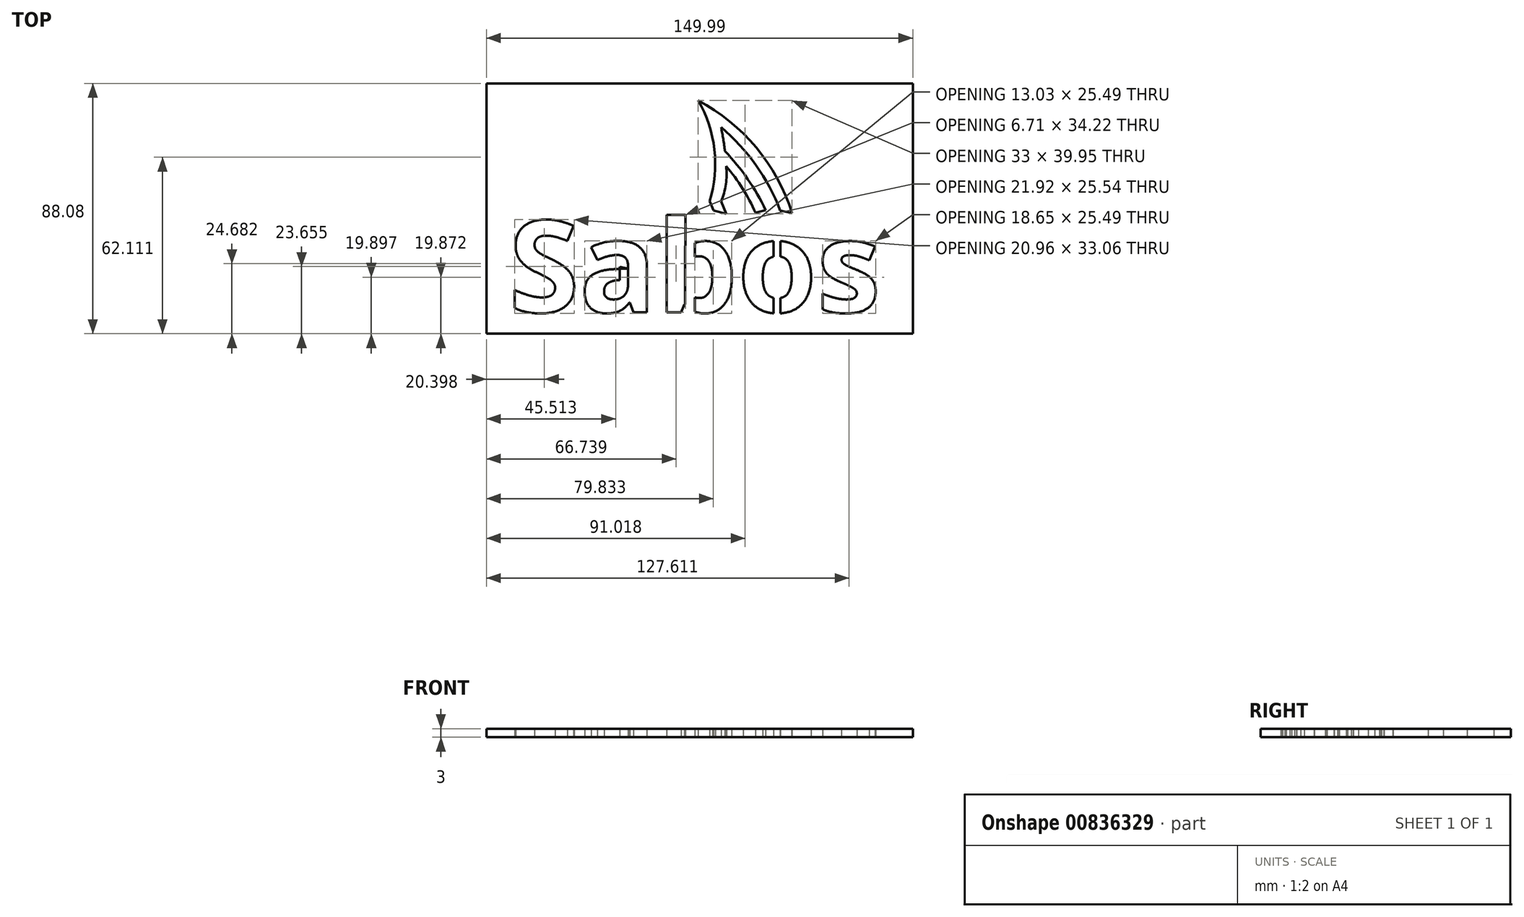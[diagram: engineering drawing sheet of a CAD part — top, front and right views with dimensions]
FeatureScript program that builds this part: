
annotation { "Feature Type Name" : "Feature", "Feature Type Description" : "" }
export const myFeature = defineFeature(function(context is Context, id is Id, definition is map)
    precondition{}
    {
        {
            var Q0;
            Q0=qCreatedBy(makeId("Top.planeOp"),FACE);
            var sketch = newSketch(context, id + "F0", { "sketchPlane" : qUnion([Q0])});
            skText(sketch, "E0", { "text": "Sabos", "fontName": "OpenSans-Bold.ttf"});
            skLineSegment(sketch, "E1", {"start": v(7.5, -7.38) * mm, "end": v(11.9, -8.54) * mm});
            skLineSegment(sketch, "E2", {"start": v(11.9, -8.54) * mm, "end": v(10.1, -4.19) * mm});
            skLineSegment(sketch, "E3", {"start": v(7.5, -7.38) * mm, "end": v(6.07, -4.03) * mm});
            skLineSegment(sketch, "E4", {"start": v(22.19, -8.14) * mm, "end": v(25.78, -7.18) * mm});
            skLineSegment(sketch, "E5", {"start": v(30.88, -7.34) * mm, "end": v(35.03, -8.18) * mm});
            skArc(sketch, "E6", {"start": v(6.07, -4.03) * mm, "mid": v(7.74, 14.12) * mm, "end": v(2.03, 31.42) * mm});
            skArc(sketch, "E7", {"start": v(35.03, -8.18) * mm, "mid": v(22.4, 14.85) * mm, "end": v(2.03, 31.42) * mm});
            skArc(sketch, "E8", {"start": v(30.88, -7.34) * mm, "mid": v(22.34, 8.62) * mm, "end": v(10.1, 21.97) * mm});
            skArc(sketch, "E9", {"start": v(25.78, -7.18) * mm, "mid": v(19.43, 3.78) * mm, "end": v(11.42, 13.58) * mm});
            skArc(sketch, "E10", {"start": v(22.19, -8.14) * mm, "mid": v(17.61, 0.41) * mm, "end": v(11.89, 8.24) * mm});
            skArc(sketch, "E11", {"start": v(11.42, 13.58) * mm, "mid": v(10.85, 17.79) * mm, "end": v(10.1, 21.97) * mm});
            skArc(sketch, "E12", {"start": v(10.1, -4.19) * mm, "mid": v(11.78, 1.91) * mm, "end": v(11.89, 8.24) * mm});
            skLineSegment(sketch, "E13.bottom", {"start": v(-72.5, -50.67) * mm, "end": v(77.5, -50.67) * mm});
            skLineSegment(sketch, "E13.top", {"start": v(-72.5, 37.4) * mm, "end": v(77.5, 37.4) * mm});
            skLineSegment(sketch, "E13.left", {"start": v(-72.5, -50.67) * mm, "end": v(-72.5, 37.4) * mm});
            skLineSegment(sketch, "E13.right", {"start": v(77.5, -50.67) * mm, "end": v(77.5, 37.4) * mm});
            skLineSegment(sketch, "E14", {"start": v(-22.68, -27.79) * mm, "end": v(-22.68, -32.66) * mm});
            skLineSegment(sketch, "E15", {"start": v(-22.68, -32.66) * mm, "end": v(-25.59, -32.66) * mm});
            skLineSegment(sketch, "E16", {"start": v(-25.59, -32.66) * mm, "end": v(-25.59, -27.2) * mm});
            skLineSegment(sketch, "E17", {"start": v(-25.59, -27.2) * mm, "end": v(-22.68, -27.79) * mm});
            skLineSegment(sketch, "E18", {"start": v(-2.57, -17.96) * mm, "end": v(-2.57, -45.1) * mm});
            skLineSegment(sketch, "E19", {"start": v(-2.57, -45.1) * mm, "end": v(0.83, -45.77) * mm});
            skLineSegment(sketch, "E20", {"start": v(0.83, -45.77) * mm, "end": v(0.83, -17.64) * mm});
            skLineSegment(sketch, "E21", {"start": v(0.83, -17.64) * mm, "end": v(-2.57, -17.96) * mm});
            skLineSegment(sketch, "E22", {"start": v(29.75, -15.5) * mm, "end": v(29.75, -46.16) * mm, "construction": true});
            skLineSegment(sketch, "E23", {"start": v(29.75, -15.5) * mm, "end": v(28.6, -15.5) * mm});
            skLineSegment(sketch, "E24", {"start": v(28.6, -15.5) * mm, "end": v(28.6, -46.25) * mm});
            skLineSegment(sketch, "E25", {"start": v(28.6, -46.25) * mm, "end": v(29.75, -46.16) * mm});
            skLineSegment(sketch, "E26.MirrorCS", {"start": v(30.9, -15.5) * mm, "end": v(30.9, -46.25) * mm});
            skLineSegment(sketch, "E27.MirrorCS", {"start": v(29.75, -15.5) * mm, "end": v(30.9, -15.5) * mm});
            skLineSegment(sketch, "E28.MirrorCS", {"start": v(30.9, -46.25) * mm, "end": v(29.75, -46.16) * mm});
            const initialGuessF0  = {"E0": [-0.06464, -0.0431, 1, 0, 0.03243]};
            skSetInitialGuess(sketch, initialGuessF0);
            skSolve(sketch);
        }
        {
            var Q0;
            {var subQ1=sQuery(id+"F0.wireOp",EDGE,"E0.sketch_text.stroke-68");Q0=makeQuery(id+"F0.imprint","IMPRINT",FACE,{"disambiguationData":[TD([[makeQuery(id+"F0.imprint","IMPRINT",EDGE,{"derivedFrom":subQ1}),1.0]])]});}
            var Q1;
            {var subQ8=sQuery(id+"F0.wireOp",EDGE,"E0.sketch_text.stroke-68");Q1=makeQuery(id+"F0.imprint","IMPRINT",FACE,{"disambiguationData":[TD([[makeQuery(id+"F0.imprint","IMPRINT",EDGE,{"derivedFrom":subQ8}),-1.0]])]});}
            var Q2;
            {var subQ1=sQuery(id+"F0.wireOp",EDGE,"E0.sketch_text.stroke-64");var subQ9=sQuery(id+"F0.wireOp",EDGE,"E21");var subQ11=makeQuery(id+"F0.imprint","INTERSECT",VERTEX,{"derivedFrom":[subQ1,subQ9]});Q2=makeQuery(id+"F0.imprint","IMPRINT",FACE,{"disambiguationData":[TD([[makeQuery(id+"F0.imprint","IMPRINT",EDGE,{"disambiguationData":[TD([[subQ11,-1.0]])],"derivedFrom":subQ1}),1.0]])]});}
            var Q3;
            {var subQ0=sQuery(id+"F0.wireOp",EDGE,"E19");Q3=makeQuery(id+"F0.imprint","IMPRINT",FACE,{"disambiguationData":[TD([[makeQuery(id+"F0.imprint","IMPRINT",EDGE,{"derivedFrom":subQ0}),1.0]])]});}
            var Q4;
            {var subQ5=sQuery(id+"F0.wireOp",EDGE,"E0.sketch_text.stroke-77");var subQ9=sQuery(id+"F0.wireOp",EDGE,"E0.sketch_text.stroke-78");var subQ10=makeQuery(id+"F0.imprint","INTERSECT",VERTEX,{"derivedFrom":[subQ5,subQ9]});Q4=makeQuery(id+"F0.imprint","IMPRINT",FACE,{"disambiguationData":[TD([[makeQuery(id+"F0.imprint","IMPRINT",EDGE,{"disambiguationData":[TD([[subQ10,1.0]])],"derivedFrom":subQ5}),-1.0]])]});}
            var Q5;
            {var subQ0=sQuery(id+"F0.wireOp",EDGE,"E25");Q5=makeQuery(id+"F0.imprint","IMPRINT",FACE,{"disambiguationData":[TD([[makeQuery(id+"F0.imprint","IMPRINT",EDGE,{"derivedFrom":subQ0}),1.0]])]});}
            var Q6;
            {var subQ7=sQuery(id+"F0.wireOp",EDGE,"E0.sketch_text.stroke-82");var subQ8=sQuery(id+"F0.wireOp",EDGE,"E0.sketch_text.stroke-81");var subQ9=makeQuery(id+"F0.imprint","INTERSECT",VERTEX,{"derivedFrom":[subQ8,subQ7]});Q6=makeQuery(id+"F0.imprint","IMPRINT",FACE,{"disambiguationData":[TD([[makeQuery(id+"F0.imprint","IMPRINT",EDGE,{"disambiguationData":[TD([[subQ9,1.0]])],"derivedFrom":subQ8}),-1.0]])]});}
            var Q7;
            {var subQ1=sQuery(id+"F0.wireOp",EDGE,"E23");Q7=makeQuery(id+"F0.imprint","IMPRINT",FACE,{"disambiguationData":[TD([[makeQuery(id+"F0.imprint","IMPRINT",EDGE,{"derivedFrom":subQ1}),1.0]])]});}
            var Q8;
            Q8=makeQuery(id+"F0.imprint","IMPRINT",FACE,{"disambiguationData":[TD([[makeQuery(id+"F0.imprint","IMPRINT",EDGE,{"derivedFrom":sQuery(id+"F0.wireOp",EDGE,"E0.sketch_text.stroke-0")}),1.0]])]});
            var Q9;
            {var subQ0=sQuery(id+"F0.wireOp",EDGE,"E0.sketch_text.stroke-37");var subQ1=sQuery(id+"F0.wireOp",EDGE,"E0.sketch_text.stroke-36");var subQ2=makeQuery(id+"F0.imprint","INTERSECT",VERTEX,{"derivedFrom":[subQ1,subQ0]});Q9=makeQuery(id+"F0.imprint","IMPRINT",FACE,{"disambiguationData":[TD([[makeQuery(id+"F0.imprint","IMPRINT",EDGE,{"disambiguationData":[TD([[subQ2,1.0]])],"derivedFrom":subQ1}),1.0]])]});}
            var Q10;
            {var subQ1=sQuery(id+"F0.wireOp",EDGE,"E0.sketch_text.stroke-46");Q10=makeQuery(id+"F0.imprint","IMPRINT",FACE,{"disambiguationData":[TD([[makeQuery(id+"F0.imprint","IMPRINT",EDGE,{"derivedFrom":subQ1}),-1.0]])]});}
            var Q11;
            {var subQ1=sQuery(id+"F0.wireOp",EDGE,"E0.sketch_text.stroke-46");Q11=makeQuery(id+"F0.imprint","IMPRINT",FACE,{"disambiguationData":[TD([[makeQuery(id+"F0.imprint","IMPRINT",EDGE,{"derivedFrom":subQ1}),1.0]])]});}
            var Q12;
            {var subQ0=sQuery(id+"F0.wireOp",EDGE,"E0.sketch_text.stroke-48");Q12=makeQuery(id+"F0.imprint","IMPRINT",FACE,{"disambiguationData":[TD([[makeQuery(id+"F0.imprint","IMPRINT",EDGE,{"derivedFrom":subQ0}),1.0]])]});}
            var Q13;
            {var subQ4=sQuery(id+"F0.wireOp",EDGE,"E0.sketch_text.stroke-79");Q13=makeQuery(id+"F0.imprint","IMPRINT",FACE,{"disambiguationData":[TD([[makeQuery(id+"F0.imprint","IMPRINT",EDGE,{"derivedFrom":subQ4}),1.0]])]});}
            var Q14;
            {var subQ1=sQuery(id+"F0.wireOp",EDGE,"E0.sketch_text.stroke-76");Q14=makeQuery(id+"F0.imprint","IMPRINT",FACE,{"disambiguationData":[TD([[makeQuery(id+"F0.imprint","IMPRINT",EDGE,{"derivedFrom":subQ1}),1.0]])]});}
            var Q15;
            {var subQ6=sQuery(id+"F0.wireOp",EDGE,"E0.sketch_text.stroke-78");var subQ9=sQuery(id+"F0.wireOp",EDGE,"E0.sketch_text.stroke-77");var subQ10=makeQuery(id+"F0.imprint","INTERSECT",VERTEX,{"derivedFrom":[subQ9,subQ6]});Q15=makeQuery(id+"F0.imprint","IMPRINT",FACE,{"disambiguationData":[TD([[makeQuery(id+"F0.imprint","IMPRINT",EDGE,{"disambiguationData":[TD([[subQ10,1.0]])],"derivedFrom":subQ9}),1.0]])]});}
            var Q16;
            {var subQ0=sQuery(id+"F0.wireOp",EDGE,"E0.sketch_text.stroke-72");Q16=makeQuery(id+"F0.imprint","IMPRINT",FACE,{"disambiguationData":[TD([[makeQuery(id+"F0.imprint","IMPRINT",EDGE,{"derivedFrom":subQ0}),1.0]])]});}
            extrude(context, id + "F1", {"entities" : qUnion([Q0, Q1, Q2, Q3, Q4, Q5, Q6, Q7, Q8, Q9, Q10, Q11, Q12, Q13, Q14, Q15, Q16]), "depth" : 3 * mm, "offsetDistance" : 25 * mm});
        }
    });
